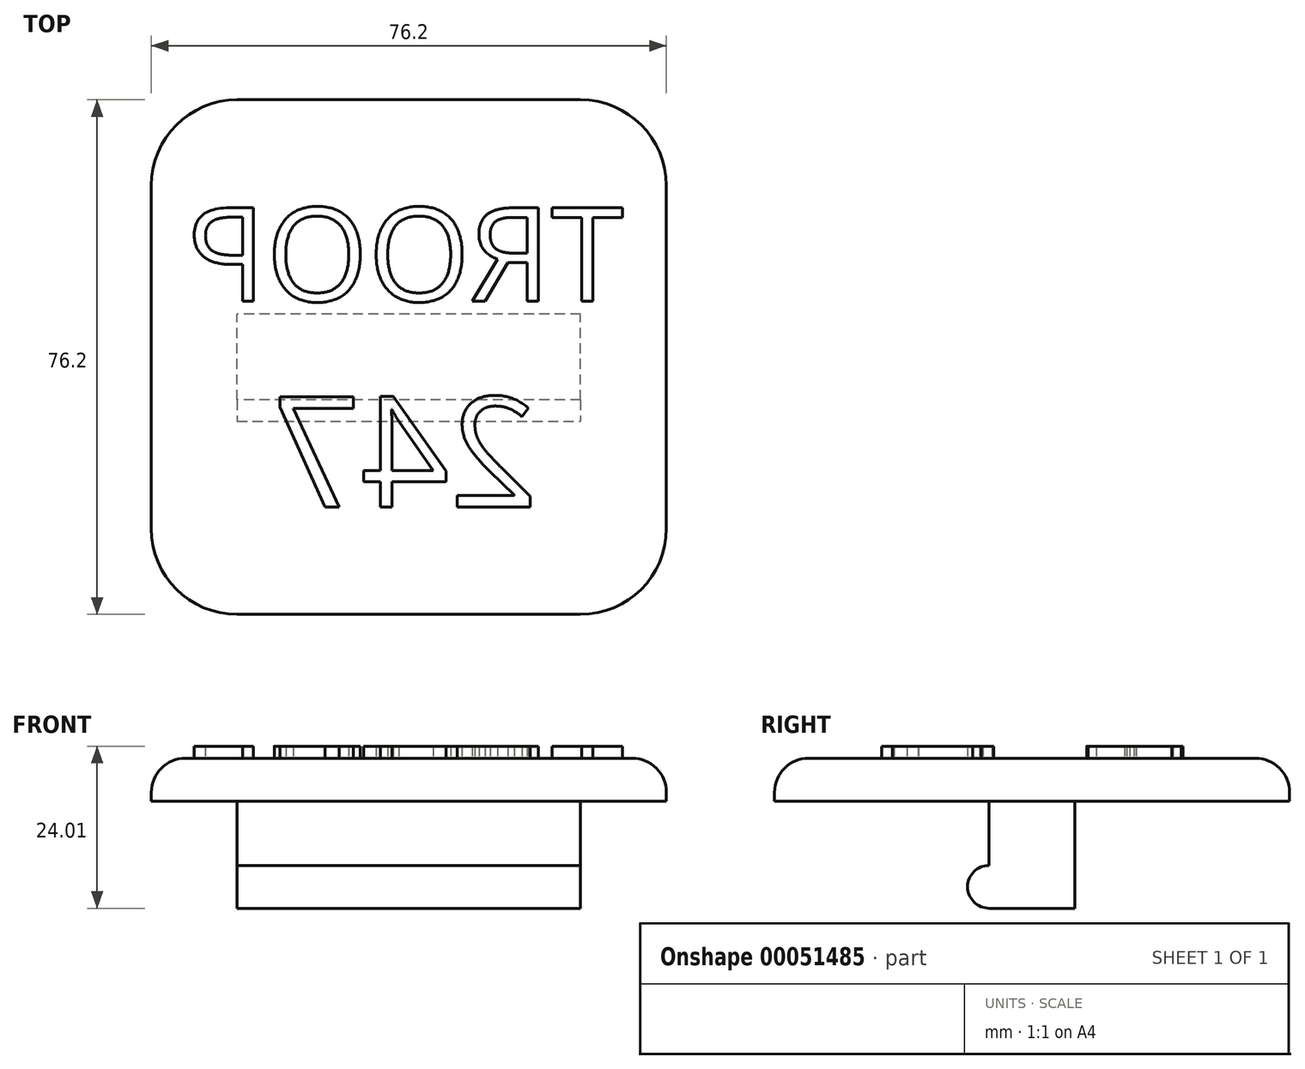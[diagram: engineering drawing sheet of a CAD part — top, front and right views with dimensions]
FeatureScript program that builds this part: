
annotation { "Feature Type Name" : "Feature", "Feature Type Description" : "" }
export const myFeature = defineFeature(function(context is Context, id is Id, definition is map)
    precondition{}
    {
        {
            var Q0;
            Q0=qCreatedBy(makeId("Top.planeOp"),FACE);
            var sketch = newSketch(context, id + "F0", { "sketchPlane" : qUnion([Q0])});
            skLineSegment(sketch, "E0.bottom", {"start": v(0, 0) * mm, "end": v(76.2, 0) * mm});
            skLineSegment(sketch, "E0.top", {"start": v(0, -76.2) * mm, "end": v(76.2, -76.2) * mm});
            skLineSegment(sketch, "E0.left", {"start": v(0, 0) * mm, "end": v(0, -76.2) * mm});
            skLineSegment(sketch, "E0.right", {"start": v(76.2, 0) * mm, "end": v(76.2, -76.2) * mm});
            skSolve(sketch);
        }
        {
            var Q0;
            Q0=makeQuery(id+"F0.imprint","IMPRINT",FACE,{"disambiguationData":[TD([[makeQuery(id+"F0.imprint","IMPRINT",EDGE,{"derivedFrom":sQuery(id+"F0.wireOp",EDGE,"E0.bottom")}),-1.0]])]});
            extrude(context, id + "F1", {"entities" : qUnion([Q0]), "depth" : 6.35 * mm});
        }
        {
            var Q0;
            Q0=makeQuery(id+"F1.opExtrude","SWEPT_EDGE",EDGE,{"disambiguationData":[OSD([sQuery(id+"F0.wireOp",EDGE,"E0.top"),sQuery(id+"F0.wireOp",EDGE,"E0.left")])]});
            var Q1;
            Q1=makeQuery(id+"F1.opExtrude","SWEPT_EDGE",EDGE,{"disambiguationData":[OSD([sQuery(id+"F0.wireOp",EDGE,"E0.top"),sQuery(id+"F0.wireOp",EDGE,"E0.right")])]});
            var Q2;
            Q2=makeQuery(id+"F1.opExtrude","SWEPT_EDGE",EDGE,{"disambiguationData":[OSD([sQuery(id+"F0.wireOp",EDGE,"E0.bottom"),sQuery(id+"F0.wireOp",EDGE,"E0.right")])]});
            var Q3;
            Q3=makeQuery(id+"F1.opExtrude","SWEPT_EDGE",EDGE,{"disambiguationData":[OSD([sQuery(id+"F0.wireOp",EDGE,"E0.bottom"),sQuery(id+"F0.wireOp",EDGE,"E0.left")])]});
            fillet(context, id + "F2", {"entities" : qUnion([Q0, Q1, Q2, Q3]), "radius" : 12.7 * mm, "tangentPropagation" : true, "allowEdgeOverflow" : false});
        }
        {
            var Q0;
            Q0=makeQuery(id+"F1.opExtrude","CAP_FACE",FACE,{"disambiguationData":[OSD([sQuery(id+"F0.wireOp",EDGE,"E0.bottom"),sQuery(id+"F0.wireOp",EDGE,"E0.top"),sQuery(id+"F0.wireOp",EDGE,"E0.left"),sQuery(id+"F0.wireOp",EDGE,"E0.right")])],"isStart":false});
            var sketch = newSketch(context, id + "F3", { "sketchPlane" : qUnion([Q0])});
            skText(sketch, "E1", { "text": "TROOP", "fontName": "OpenSans-Regular.ttf"});
            skText(sketch, "E2", { "text": "247", "fontName": "OpenSans-Regular.ttf"});
            const initialGuessF3  = {"E1": [0.00635, -0.02982, 1, 0, 0.01394], "E2": [0.01905, -0.06033, 1, 0, 0.01648]};
            skSetInitialGuess(sketch, initialGuessF3);
            skSolve(sketch);
        }
        {
            var Q0;
            Q0 = qSketchRegion(id + "F3", true);
            extrude(context, id + "F4", {"entities" : qUnion([Q0]), "operationType" : NewBodyOperationType.ADD, "depth" : 1.78 * mm});
        }
        {
            var Q0;
            {var subQ0=sQuery(id+"F0.wireOp",EDGE,"E0.left");var subQ1=sQuery(id+"F0.wireOp",EDGE,"E0.top");Q0=makeQuery(id+"F2.opFillet","BLEND_EDGE",EDGE,{"blendedFrom":[makeQuery(id+"F1.opExtrude","SWEPT_EDGE",EDGE,{"disambiguationData":[OSD([subQ1,subQ0])]}),makeQuery(id+"F1.opExtrude","CAP_FACE",FACE,{"disambiguationData":[OSD([sQuery(id+"F0.wireOp",EDGE,"E0.bottom"),subQ1,subQ0,sQuery(id+"F0.wireOp",EDGE,"E0.right")])],"isStart":false})],"blendedInto":[makeQuery(id+"F1.opExtrude","CAP_FACE",FACE,{"disambiguationData":[OSD([sQuery(id+"F0.wireOp",EDGE,"E0.bottom"),subQ1,subQ0,sQuery(id+"F0.wireOp",EDGE,"E0.right")])],"isStart":false})]});}
            fillet(context, id + "F5", {"entities" : qUnion([Q0]), "radius" : 5.08 * mm, "tangentPropagation" : true, "allowEdgeOverflow" : false});
        }
        {
            var Q0;
            Q0=makeQuery(id+"F1.opExtrude","CAP_FACE",FACE,{"disambiguationData":[OSD([sQuery(id+"F0.wireOp",EDGE,"E0.bottom"),sQuery(id+"F0.wireOp",EDGE,"E0.top"),sQuery(id+"F0.wireOp",EDGE,"E0.left"),sQuery(id+"F0.wireOp",EDGE,"E0.right")])],"isStart":true});
            var sketch = newSketch(context, id + "F6", { "sketchPlane" : qUnion([Q0])});
            skLineSegment(sketch, "E3.bottom", {"start": v(12.7, 44.45) * mm, "end": v(63.5, 44.45) * mm});
            skLineSegment(sketch, "E3.top", {"start": v(12.7, 31.75) * mm, "end": v(63.5, 31.75) * mm});
            skLineSegment(sketch, "E3.left", {"start": v(12.7, 44.45) * mm, "end": v(12.7, 31.75) * mm});
            skLineSegment(sketch, "E3.right", {"start": v(63.5, 44.45) * mm, "end": v(63.5, 31.75) * mm});
            skSolve(sketch);
        }
        {
            var Q0;
            Q0=makeQuery(id+"F6.imprint","IMPRINT",FACE,{"disambiguationData":[TD([[makeQuery(id+"F6.imprint","IMPRINT",EDGE,{"derivedFrom":sQuery(id+"F6.wireOp",EDGE,"E3.bottom")}),-1.0]])]});
            extrude(context, id + "F7", {"entities" : qUnion([Q0]), "operationType" : NewBodyOperationType.ADD, "depth" : 15.88 * mm});
        }
        {
            var Q0;
            Q0=makeQuery(id+"F7.opExtrude","SWEPT_FACE",FACE,{"disambiguationData":[OSD([sQuery(id+"F6.wireOp",EDGE,"E3.left")])]});
            var sketch = newSketch(context, id + "F8", { "sketchPlane" : qUnion([Q0])});
            skArc(sketch, "E4", {"start": v(44.45, -15.88) * mm, "mid": v(47.62, -12.7) * mm, "end": v(44.45, -9.52) * mm});
            skLineSegment(sketch, "E5", {"start": v(38.1, -15.88) * mm, "end": v(38.1, 0) * mm, "construction": true});
            skLineSegment(sketch, "E6", {"start": v(44.45, -15.88) * mm, "end": v(44.45, -9.52) * mm});
            skArc(sketch, "E7.MirrorCS", {"start": v(31.75, -15.88) * mm, "mid": v(28.58, -12.7) * mm, "end": v(31.75, -9.52) * mm});
            skLineSegment(sketch, "E8.MirrorCS", {"start": v(31.75, -15.88) * mm, "end": v(31.75, -9.52) * mm});
            skSolve(sketch);
        }
        {
            var Q0;
            Q0=makeQuery(id+"F8.imprint","IMPRINT",FACE,{"disambiguationData":[TD([[makeQuery(id+"F8.imprint","IMPRINT",EDGE,{"derivedFrom":sQuery(id+"F8.wireOp",EDGE,"E4")}),1.0]])]});
            var Q1;
            Q1=makeQuery(id+"F8.imprint","IMPRINT",FACE,{"disambiguationData":[TD([[makeQuery(id+"F8.imprint","IMPRINT",EDGE,{"derivedFrom":sQuery(id+"F8.wireOp",EDGE,"E7.MirrorCS")}),-1.0]])]});
            var Q2;
            Q2=makeQuery(id+"F7.opExtrude","SWEPT_FACE",FACE,{"disambiguationData":[OSD([sQuery(id+"F6.wireOp",EDGE,"E3.right")])]});
            extrude(context, id + "F9", {"entities" : qUnion([Q0, Q1]), "operationType" : NewBodyOperationType.ADD, "endBound" : BoundingType.UP_TO_SURFACE, "oppositeDirection" : true, "endBoundEntityFace" : qUnion([Q2]), "depth" : 25.4 * mm});
        }
        {
            var Q0;
            Q0=makeQuery(id+"F1.opExtrude","SWEPT_BODY",BODY,{"disambiguationData":[OSD([sQuery(id+"F0.wireOp",EDGE,"E0.bottom"),sQuery(id+"F0.wireOp",EDGE,"E0.top"),sQuery(id+"F0.wireOp",EDGE,"E0.left"),sQuery(id+"F0.wireOp",EDGE,"E0.right")])]});
            var Q1;
            Q1=qCreatedBy(makeId("Right.planeOp"),FACE);
            mirror(context, id + "F10", {"entities" : qUnion([Q0]), "mirrorPlane" : qUnion([Q1])});
        }
        {
            var Q0;
            Q0=makeQuery(id+"F1.opExtrude","SWEPT_BODY",BODY,{"disambiguationData":[OSD([sQuery(id+"F0.wireOp",EDGE,"E0.bottom"),sQuery(id+"F0.wireOp",EDGE,"E0.top"),sQuery(id+"F0.wireOp",EDGE,"E0.left"),sQuery(id+"F0.wireOp",EDGE,"E0.right")])]});
            deleteBodies(context, id + "F11", {"entities" : qUnion([Q0])});
        }
    });
